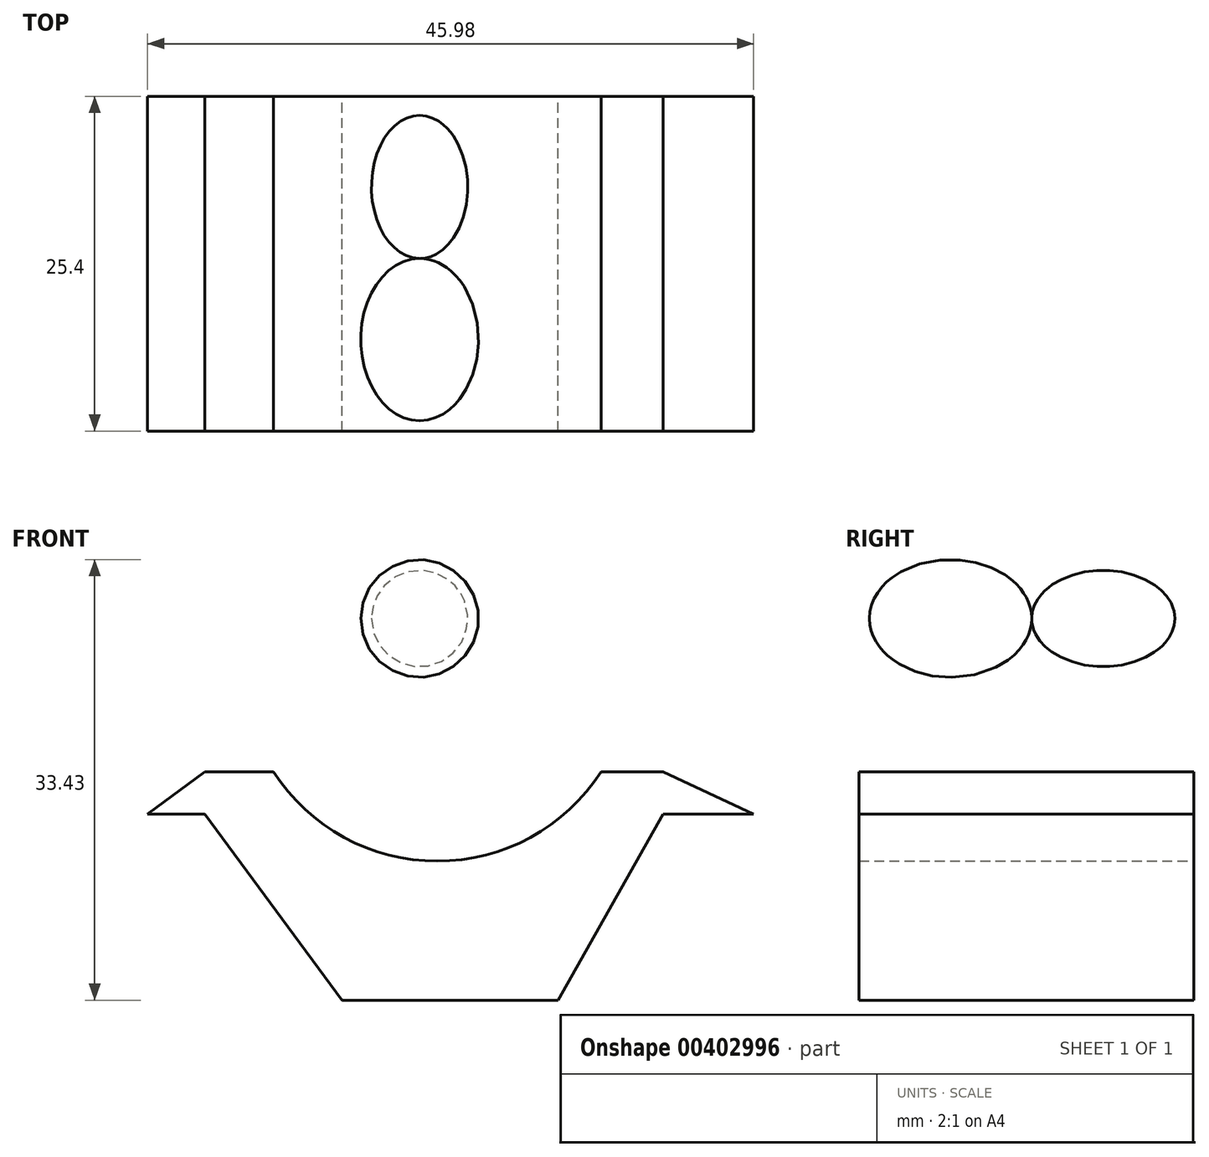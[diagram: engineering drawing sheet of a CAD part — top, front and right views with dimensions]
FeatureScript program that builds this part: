
annotation { "Feature Type Name" : "Feature", "Feature Type Description" : "" }
export const myFeature = defineFeature(function(context is Context, id is Id, definition is map)
    precondition{}
    {
        {
            var Q0;
            Q0=qCreatedBy(makeId("Front.planeOp"),FACE);
            var sketch = newSketch(context, id + "F0", { "sketchPlane" : qUnion([Q0])});
            skLineSegment(sketch, "E0", {"start": v(-26.8, -14.84) * mm, "end": v(-16.37, -28.96) * mm});
            skPoint(sketch, "E1.end.orphan", {"position": v(0, -28.96) * mm});
            skPoint(sketch, "E1.start.orphan", {"position": v(-5.8, -28.96) * mm});
            skLineSegment(sketch, "E2", {"start": v(-16.37, -28.96) * mm, "end": v(0, -28.96) * mm});
            skLineSegment(sketch, "E3", {"start": v(0, -28.96) * mm, "end": v(7.96, -14.84) * mm});
            skLineSegment(sketch, "E4", {"start": v(-26.8, -14.84) * mm, "end": v(-31.14, -14.84) * mm});
            skLineSegment(sketch, "E5", {"start": v(-31.14, -14.84) * mm, "end": v(-26.8, -11.64) * mm});
            skLineSegment(sketch, "E6", {"start": v(-26.8, -11.64) * mm, "end": v(-21.58, -11.64) * mm});
            skLineSegment(sketch, "E7", {"start": v(3.26, -11.64) * mm, "end": v(7.96, -11.64) * mm});
            skLineSegment(sketch, "E8", {"start": v(7.96, -11.64) * mm, "end": v(14.84, -14.84) * mm});
            skLineSegment(sketch, "E9", {"start": v(14.84, -14.84) * mm, "end": v(0.47, -14.84) * mm});
            skArc(sketch, "E10", {"start": v(-21.58, -11.64) * mm, "mid": v(-9.16, -18.41) * mm, "end": v(3.26, -11.64) * mm});
            skLineSegment(sketch, "E11.trimOffspring", {"start": v(-18.79, -14.84) * mm, "end": v(-26.8, -14.84) * mm});
            skPoint(sketch, "E12.orphan", {"position": v(-16.37, -11.64) * mm});
            skSolve(sketch);
        }
        {
            var Q0;
            Q0 = qSketchRegion(id + "F0", true);
            extrude(context, id + "F1", {"entities" : qUnion([Q0]), "depth" : 25.4 * mm});
        }
        {
            var Q0;
            Q0=qCreatedBy(makeId("Top.planeOp"),FACE);
            var sketch = newSketch(context, id + "F2", { "sketchPlane" : qUnion([Q0])});
            skEllipse(sketch, "E13", {"center": v(-10.5, -6.88) * mm, "majorRadius": 5.43 * mm, "minorRadius": 3.65 * mm, "majorAxis": v(0, 1)});
            skEllipse(sketch, "E14", {"center": v(-10.5, -18.46) * mm, "majorRadius": 6.15 * mm, "minorRadius": 4.47 * mm, "majorAxis": v(0, 1)});
            skLineSegment(sketch, "E15", {"start": v(-10.5, -1.45) * mm, "end": v(-10.5, -24.62) * mm});
            skSolve(sketch);
        }
        {
            var Q0;
            {var subQ0=sQuery(id+"F2.wireOp",EDGE,"E15");var subQ1=sQuery(id+"F2.wireOp",EDGE,"E13");var subQ2=makeQuery(id+"F2.imprint","INTERSECT",VERTEX,{"derivedFrom":[subQ1,subQ0]});Q0=makeQuery(id+"F2.imprint","IMPRINT",FACE,{"disambiguationData":[TD([[makeQuery(id+"F2.imprint","IMPRINT",EDGE,{"disambiguationData":[TD([[subQ2,-1.0]])],"derivedFrom":subQ1}),1.0]])]});}
            var Q1;
            {var subQ0=sQuery(id+"F2.wireOp",EDGE,"E15");var subQ1=sQuery(id+"F2.wireOp",EDGE,"E14");var subQ2=makeQuery(id+"F2.imprint","INTERSECT",VERTEX,{"derivedFrom":[subQ1,subQ0]});Q1=makeQuery(id+"F2.imprint","IMPRINT",FACE,{"disambiguationData":[TD([[makeQuery(id+"F2.imprint","IMPRINT",EDGE,{"disambiguationData":[TD([[subQ2,1.0]])],"derivedFrom":subQ1}),1.0]])]});}
            var Q2;
            Q2=sQuery(id+"F2.wireOp",EDGE,"E15");
            revolve(context, id + "F3", {"entities" : qUnion([Q0, Q1]), "axis" : qUnion([Q2]), "revolveType" : RevolveType.FULL});
        }
    });
